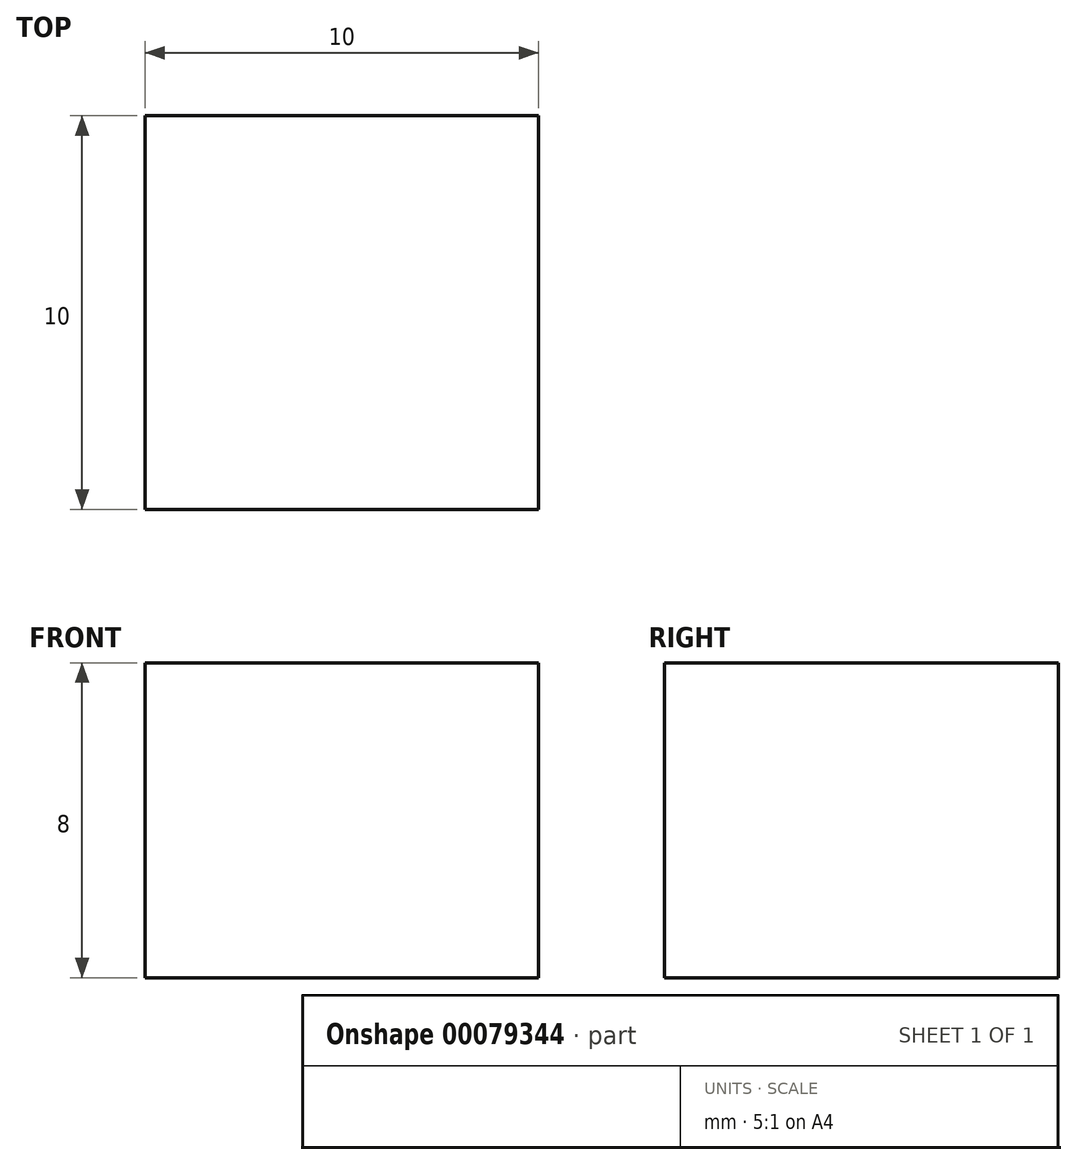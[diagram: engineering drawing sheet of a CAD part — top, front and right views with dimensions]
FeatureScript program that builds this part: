
annotation { "Feature Type Name" : "Feature", "Feature Type Description" : "" }
export const myFeature = defineFeature(function(context is Context, id is Id, definition is map)
    precondition{}
    {
        {
            var Q0;
            Q0=qCreatedBy(makeId("Top.planeOp"),FACE);
            var sketch = newSketch(context, id + "F0", { "sketchPlane" : qUnion([Q0])});
            skLineSegment(sketch, "E0.bottom", {"start": v(0, 0) * mm, "end": v(10, 0) * mm});
            skLineSegment(sketch, "E0.top", {"start": v(0, 10) * mm, "end": v(10, 10) * mm});
            skLineSegment(sketch, "E0.left", {"start": v(0, 0) * mm, "end": v(0, 10) * mm});
            skLineSegment(sketch, "E0.right", {"start": v(10, 0) * mm, "end": v(10, 10) * mm});
            skSolve(sketch);
        }
        {
            var Q0;
            Q0 = qSketchRegion(id + "F0", true);
            extrude(context, id + "F1", {"entities" : qUnion([Q0]), "depth" : 8 * mm});
        }
    });
